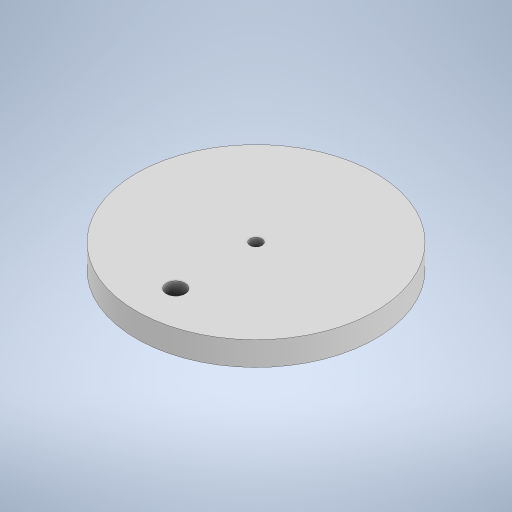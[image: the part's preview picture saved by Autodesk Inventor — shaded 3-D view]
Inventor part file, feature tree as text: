
AUTODESK INVENTOR PART (.ipt)
format: ipt  version: 2023 (Build 270158000, 158)  size: 259,584 bytes
history: native  units: mm
features: extrude x1, sketch x1
ambient origin geometry x8: Origin, YZ Plane, XZ Plane, XY Plane, X Axis, Y Axis, Z Axis, Center Point
bodies: Solid1 (feature_tree)
feature tree (2):
  extrude  "Extrusion1"  Depth=8.0mm
  sketch  "Sketch1"  dims[d1=120.0mm d2=200.0mm d3=15.0deg d4=10.0mm d5=10.0mm d6=79.8mm d7=360.0deg d8=10.0mm d9=4.0mm d10=6.3mm d11=8.0mm d12=0.0mm d13=0.5mm d14=0.872665mm]
